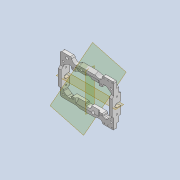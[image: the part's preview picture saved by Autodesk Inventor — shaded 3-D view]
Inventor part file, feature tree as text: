
AUTODESK INVENTOR PART (.ipt)
format: ipt  version: 2020 (Build 240168000, 168)  size: 979,968 bytes
history: native  units: mm
features: sketch x22, extrude x20, projected_geometry x20, reference x17, fillet x14, other x12, mirror x8, thicken_offset x8, plane x3, chamfer x3, hole x2
ambient origin geometry x8: Origin, YZ Plane, XZ Plane, XY Plane, X Axis, Y Axis, Z Axis, Center Point
bodies: Solid1 (feature_tree)
feature tree (129):
  extrude  "Extrusion1"  Depth=30.0mm
  extrude  "Extrusion2"  Depth=56.0mm
  plane  "Work Plane1"
  mirror  "Mirror1"
  extrude  "Extrusion3"  Depth=20.0mm
  extrude  "Extrusion4"  Depth=4.0mm TaperAngle=0.0deg
  plane  "Work Plane2"
  extrude  "Extrusion5"  Depth=10.0mm
  extrude  "Extrusion6"  Depth=1.5mm
  plane  "Work Plane3"
  mirror  "Mirror2"
  extrude  "Extrusion7"  Depth=1.0mm TaperAngle=0.0deg
  mirror  "Mirror3"
  fillet  "Fillet1"  Radius=1.0mm
  thicken_offset  "Thicken1"
  thicken_offset  "Thicken2"
  extrude  "Extrusion8"  Depth=6.0mm TaperAngle=0.0deg
  mirror  "Mirror4"
  extrude  "Extrusion10"  Depth=10.0mm
  thicken_offset  "Thicken3"
  mirror  "Mirror5"
  thicken_offset  "Thicken4"
  extrude  "Extrusion11"  Depth=3.5mm
  extrude  "Extrusion12"  Depth=10.0mm TaperAngle=0.0deg
  fillet  "Fillet4"  Radius=8.0mm
  extrude  "Extrusion13"  Depth=1.0mm
  extrude  "Extrusion14"  Depth=1.0mm
  extrude  "Extrusion15"  Depth=4.0mm
  extrude  "Extrusion16"  Depth=1.0mm
  thicken_offset  "Thicken5"
  fillet  "Fillet7"  Radius=1.5mm
  fillet  "Fillet8"  Radius=4.0mm
  fillet  "Fillet9"  Radius=3.0mm
  fillet  "Fillet10"  Radius=10.0mm
  fillet  "Fillet11"  Radius=4.0mm
  fillet  "Fillet12"  Radius=1.0mm
  extrude  "Extrusion17"  Depth=0.5mm
  mirror  "Mirror6"
  extrude  "Extrusion18"  Depth=10.0mm
  hole  "Hole1"  [1 undecoded]
  extrude  "Extrusion19"  Depth=2.8mm
  thicken_offset  "Thicken6"
  hole  "Hole2"  [1 undecoded]
  extrude  "Extrusion20"  Depth=6.0mm TaperAngle=0.0deg
  extrude  "Extrusion21"  Depth=1.0mm
  mirror  "Mirror7"
  fillet  "Fillet13"  Radius=6.0mm
  mirror  "Mirror8"
  fillet  "Fillet14"  Radius=15.0mm
  fillet  "Fillet15"  Radius=2.8mm
  chamfer  "Chamfer1"  Distance=6.0mm
  fillet  "Fillet16"  Radius=1.5mm
  chamfer  "Chamfer2"  Distance=1.5mm
  chamfer  "Chamfer3"  Distance=4.0mm
  fillet  "Fillet17"  Radius=3.0mm
  fillet  "Fillet18"  Radius=4.0mm
  thicken_offset  "Thicken7"
  thicken_offset  "Thicken8"
  sketch  "Sketch1"  dims[d0=50.0mm d1=30.0mm]
  reference  "Reference1"
  reference  "Reference2"
  sketch  "Sketch2"  dims[d2=36.0mm d3=56.0mm]
  projected_geometry  "Projected Loop1"
  reference  "Reference3"
  sketch  "Sketch3"  dims[d4=4.0mm d5=0.0mm d6=20.0mm]
  reference  "Reference4"
  sketch  "Sketch4"  dims[d7=8.0mm d8=4.0mm d9=0.0mm]
  reference  "Reference5"
  reference  "Reference6"
  sketch  "Sketch5"  dims[d10=10.0mm d11=4.0mm]
  projected_geometry  "Projected Loop2"
  projected_geometry  "Projected Loop3"
  projected_geometry  "Projected Loop4"
  reference  "Reference7"
  sketch  "Sketch6"  dims[d12=80.0mm d13=0.0mm d14=1.5mm]
  projected_geometry  "Projected Loop5"
  projected_geometry  "Projected Loop6"
  sketch  "Sketch7"  dims[d15=1.5mm d16=80.0mm d17=0.0mm d18=1.0mm]
  projected_geometry  "Projected Loop7"
  projected_geometry  "Projected Loop8"
  sketch  "Sketch8"  dims[d19=3.0mm d20=6.0mm d21=0.0mm]
  projected_geometry  "Projected Loop9"
  reference  "Reference8"
  reference  "Reference9"
  sketch  "Sketch10"  dims[d22=10.0mm d23=0.0mm d24=3.5mm]
  projected_geometry  "Projected Loop11"
  sketch  "Sketch11"  dims[d25=5.0mm d26=3.5mm]
  projected_geometry  "Projected Loop13"
  projected_geometry  "Projected Loop14"
  sketch  "Sketch12"  dims[d27=5.0mm d28=10.0mm d29=0.0mm d30=8.0mm]
  reference  "Reference11"
  sketch  "Sketch13"  dims[d32=1.0mm d33=1.0mm]
  projected_geometry  "Projected Loop15"
  sketch  "Sketch14"  dims[d34=1.0mm d35=1.0mm]
  projected_geometry  "Projected Loop16"
  sketch  "Sketch15"  dims[d36=1.5mm d37=4.0mm]
  projected_geometry  "Projected Loop17"
  sketch  "Sketch16"  dims[d38=3.0mm d39=2.0mm d40=1.5mm d41=4.0mm d42=3.0mm d43=10.0mm d44=0.0mm d49=4.0mm d50=0.0mm d51=0.5mm d52=1.0mm]
  reference  "Reference12"
  sketch  "Sketch17"  dims[d53=0.5mm d54=0.5mm]
  projected_geometry  "Projected Loop18"
  sketch  "Sketch18"  dims[d55=10.0mm d56=0.0mm d58=29.0mm]
  reference  "Reference13"
  reference  "Reference14"
  projected_geometry  "Projected Loop19"
  sketch  "Sketch19"  dims[d59=6.0mm d60=0.0mm d61=1.0mm]
  reference  "Reference15"
  sketch  "Sketch20"  dims[d63=2.0mm d64=2.8mm]
  reference  "Reference16"
  projected_geometry  "Projected Loop20"
  sketch  "Sketch21"  dims[d65=6.0mm d66=0.0mm d67=2.0mm]
  reference  "Reference17"
  sketch  "Sketch22"  dims[d68=2.8mm d69=6.0mm d70=0.0mm]
  projected_geometry  "Projected Loop21"
  reference  "Reference18"
  sketch  "Sketch23"  dims[d71=12.0mm d72=5.0mm d73=6.0mm d74=0.0mm d76=15.0mm d78=2.8mm d79=6.0mm d80=0.0mm d81=1.5mm d82=1.5mm d83=4.0mm d84=3.0mm d85=4.0mm d86=1.0mm d87=1.5mm d88=2.0mm d89=1.0mm d90=2.0mm d91=1.1mm d92=2.0mm d93=1.1mm d94=8.0mm d95=0.0mm d96=2.8mm d97=5.0mm d98=2.8mm d99=6.0mm d100=12.0mm d101=0.0mm d102=1.1mm d103=6.0mm d104=4.0mm d105=2.0mm d106=90.0deg d107=100.0mm d108=0.0mm d109=3.0mm d110=4.0mm d111=0.0mm d112=0.005mm d113=0.005mm d114=1.1mm d115=6.0mm d116=4.0mm d117=2.0mm d118=90.0deg d119=100.0mm d120=0.0mm d121=12.0mm d122=4.5mm d123=4.0mm d124=0.0mm d125=3.0mm d126=3.0mm d127=3.0mm d128=2.0mm d129=6.0mm d130=0.0mm d131=3.0mm d132=3.0mm d133=1.0mm d134=2.5mm d135=2.0mm d136=45.0deg d137=2.0mm d138=1.0mm d139=2.0mm d140=45.0deg d141=1.0mm d142=2.0mm d143=45.0deg d144=1.0mm d145=1.0mm d146=1.0mm d147=1.0mm d148=1.0mm d149=1.0mm]
  projected_geometry  "Projected Loop22"
  parser-record x1  (decoder bookkeeping rows leaked as tree rows — omitted from the tree; the rows remain in map.json)
  other  "tip_3_ass.iam"
  other  "bearing_hh_1:1"
  other  "bearing_hh_1:2"
  other  "pin_3_30:2"
  other  "roller_1:2"
  other  "roller_1:1"
  other  "c_roller_1:2"
  other  "c_roller_1:1"
  other  "bw_ass_1:1"
  other  "bw_hl_1:1"
  other  "bw_ass_1:2"
note: 2 required parameter values undecoded (feature->parameter linkage not recoverable at this tier; creation-order binding heuristic only, values carry confidence <= 0.55)
note: 1 file-system path scrubbed to <path> (originals preserved in map.json)
